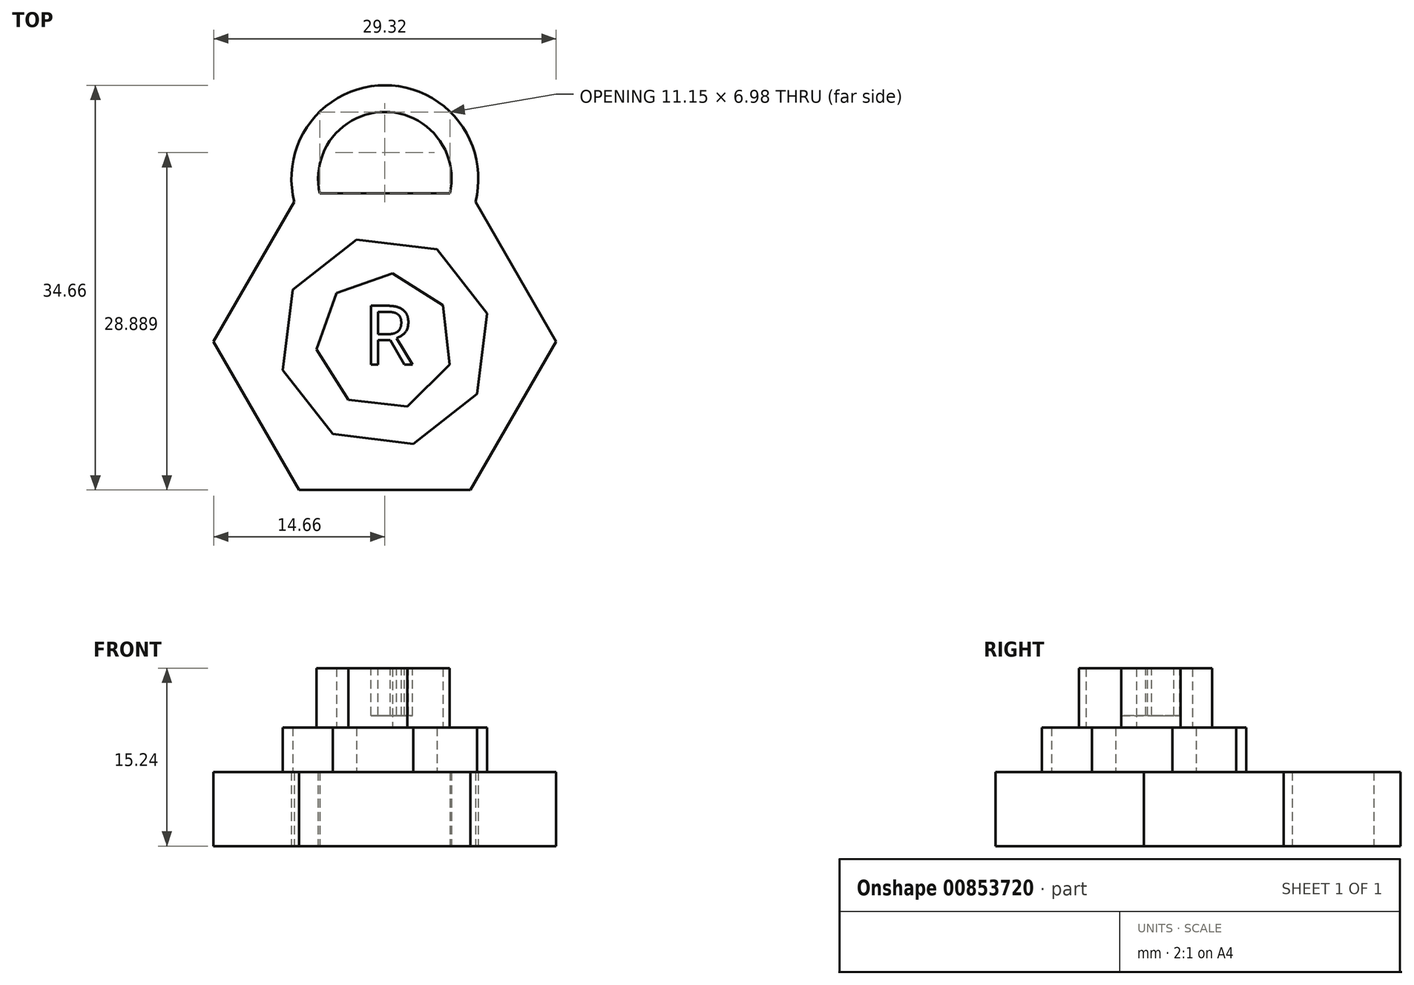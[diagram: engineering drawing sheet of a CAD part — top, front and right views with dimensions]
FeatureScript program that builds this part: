
annotation { "Feature Type Name" : "Feature", "Feature Type Description" : "" }
export const myFeature = defineFeature(function(context is Context, id is Id, definition is map)
    precondition{}
    {
        {
            var Q0;
            Q0=qCreatedBy(makeId("Top.planeOp"),FACE);
            var sketch = newSketch(context, id + "F0", { "sketchPlane" : qUnion([Q0])});
            skCircle(sketch, "E0.cCircle", {"center": v(0, 0) * mm, "radius": 12.7 * mm, "construction": true});
            skLineSegment(sketch, "E0.0", {"start": v(-7.33, 12.7) * mm, "end": v(7.33, 12.7) * mm});
            skLineSegment(sketch, "E0.1", {"start": v(7.33, 12.7) * mm, "end": v(14.66, 0) * mm});
            skLineSegment(sketch, "E0.2", {"start": v(14.66, 0) * mm, "end": v(7.33, -12.7) * mm});
            skLineSegment(sketch, "E0.3", {"start": v(7.33, -12.7) * mm, "end": v(-7.33, -12.7) * mm});
            skLineSegment(sketch, "E0.4", {"start": v(-7.33, -12.7) * mm, "end": v(-14.66, 0) * mm});
            skLineSegment(sketch, "E0.5", {"start": v(-14.66, 0) * mm, "end": v(-7.33, 12.7) * mm});
            skPoint(sketch, "E0.0.midPoint", {"position": v(0, 12.7) * mm});
            skSolve(sketch);
        }
        {
            var Q0;
            Q0=makeQuery(id+"F0.imprint","IMPRINT",FACE,{"disambiguationData":[TD([[makeQuery(id+"F0.imprint","IMPRINT",EDGE,{"derivedFrom":sQuery(id+"F0.wireOp",EDGE,"E0.0")}),-1.0]])]});
            extrude(context, id + "F1", {"entities" : qUnion([Q0]), "depth" : 6.35 * mm, "offsetDistance" : 25.4 * mm});
        }
        {
            var Q0;
            Q0=makeQuery(id+"F1.opExtrude","CAP_FACE",FACE,{"disambiguationData":[OSD([sQuery(id+"F0.wireOp",EDGE,"E0.0"),sQuery(id+"F0.wireOp",EDGE,"E0.1"),sQuery(id+"F0.wireOp",EDGE,"E0.2"),sQuery(id+"F0.wireOp",EDGE,"E0.3"),sQuery(id+"F0.wireOp",EDGE,"E0.4"),sQuery(id+"F0.wireOp",EDGE,"E0.5")])],"isStart":false});
            var sketch = newSketch(context, id + "F2", { "sketchPlane" : qUnion([Q0])});
            skCircle(sketch, "E1.cCircle", {"center": v(0, 0) * mm, "radius": 8.38 * mm, "construction": true});
            skLineSegment(sketch, "E1.0", {"start": v(7.9, -4.46) * mm, "end": v(2.44, -8.74) * mm});
            skLineSegment(sketch, "E1.1", {"start": v(2.44, -8.74) * mm, "end": v(-4.46, -7.9) * mm});
            skLineSegment(sketch, "E1.2", {"start": v(-4.46, -7.9) * mm, "end": v(-8.74, -2.44) * mm});
            skLineSegment(sketch, "E1.3", {"start": v(-8.74, -2.44) * mm, "end": v(-7.9, 4.46) * mm});
            skLineSegment(sketch, "E1.4", {"start": v(-7.9, 4.46) * mm, "end": v(-2.44, 8.74) * mm});
            skLineSegment(sketch, "E1.5", {"start": v(-2.44, 8.74) * mm, "end": v(4.46, 7.9) * mm});
            skLineSegment(sketch, "E1.6", {"start": v(4.46, 7.9) * mm, "end": v(8.74, 2.44) * mm});
            skLineSegment(sketch, "E1.7", {"start": v(8.74, 2.44) * mm, "end": v(7.9, -4.46) * mm});
            skPoint(sketch, "E1.0.midPoint", {"position": v(5.17, -6.6) * mm});
            skSolve(sketch);
        }
        {
            var Q0;
            Q0 = qSketchRegion(id + "F2", true);
            extrude(context, id + "F3", {"entities" : qUnion([Q0]), "operationType" : NewBodyOperationType.ADD, "depth" : 3.8 * mm, "offsetDistance" : 25.4 * mm});
        }
        {
            var Q0;
            Q0=makeQuery(id+"F3.opExtrude","CAP_FACE",FACE,{"disambiguationData":[OSD([sQuery(id+"F2.wireOp",EDGE,"E1.0"),sQuery(id+"F2.wireOp",EDGE,"E1.1"),sQuery(id+"F2.wireOp",EDGE,"E1.2"),sQuery(id+"F2.wireOp",EDGE,"E1.3"),sQuery(id+"F2.wireOp",EDGE,"E1.4"),sQuery(id+"F2.wireOp",EDGE,"E1.5"),sQuery(id+"F2.wireOp",EDGE,"E1.6"),sQuery(id+"F2.wireOp",EDGE,"E1.7")])],"isStart":false});
            var sketch = newSketch(context, id + "F4", { "sketchPlane" : qUnion([Q0])});
            skCircle(sketch, "E2.cCircle", {"center": v(0, 0) * mm, "radius": 5.3 * mm, "construction": true});
            skLineSegment(sketch, "E2.0", {"start": v(5.55, -1.95) * mm, "end": v(1.93, -5.55) * mm});
            skLineSegment(sketch, "E2.1", {"start": v(1.93, -5.55) * mm, "end": v(-3.13, -4.97) * mm});
            skLineSegment(sketch, "E2.2", {"start": v(-3.13, -4.97) * mm, "end": v(-5.84, -0.65) * mm});
            skLineSegment(sketch, "E2.3", {"start": v(-5.84, -0.65) * mm, "end": v(-4.15, 4.16) * mm});
            skLineSegment(sketch, "E2.4", {"start": v(-4.15, 4.16) * mm, "end": v(0.67, 5.84) * mm});
            skLineSegment(sketch, "E2.5", {"start": v(0.67, 5.84) * mm, "end": v(4.98, 3.12) * mm});
            skLineSegment(sketch, "E2.6", {"start": v(4.98, 3.12) * mm, "end": v(5.55, -1.95) * mm});
            skPoint(sketch, "E2.0.midPoint", {"position": v(3.74, -3.75) * mm});
            skSolve(sketch);
        }
        {
            var Q0;
            Q0 = qSketchRegion(id + "F4", true);
            extrude(context, id + "F5", {"entities" : qUnion([Q0]), "operationType" : NewBodyOperationType.ADD, "depth" : 5.08 * mm, "offsetDistance" : 25.4 * mm});
        }
        {
            var Q0;
            Q0=makeQuery(id+"F5.opExtrude","CAP_FACE",FACE,{"disambiguationData":[OSD([sQuery(id+"F4.wireOp",EDGE,"E2.0"),sQuery(id+"F4.wireOp",EDGE,"E2.1"),sQuery(id+"F4.wireOp",EDGE,"E2.2"),sQuery(id+"F4.wireOp",EDGE,"E2.3"),sQuery(id+"F4.wireOp",EDGE,"E2.4"),sQuery(id+"F4.wireOp",EDGE,"E2.5"),sQuery(id+"F4.wireOp",EDGE,"E2.6")])],"isStart":false});
            var sketch = newSketch(context, id + "F6", { "sketchPlane" : qUnion([Q0])});
            skText(sketch, "E3", { "text": "R", "fontName": "OpenSans-Regular.ttf"});
            skPoint(sketch, "E3.secondSnap0", {"position": v(2.82, 4.48) * mm});
            const initialGuessF6  = {"E3": [-0.00187, -0.00195, 1, 0, 0.00507]};
            skSetInitialGuess(sketch, initialGuessF6);
            skSolve(sketch);
        }
        {
            var Q0;
            Q0 = qSketchRegion(id + "F6", true);
            extrude(context, id + "F7", {"entities" : qUnion([Q0]), "operationType" : NewBodyOperationType.REMOVE, "oppositeDirection" : true, "depth" : 4.06 * mm, "offsetDistance" : 25.4 * mm});
        }
        {
            var Q0;
            Q0=makeQuery(id+"F1.opExtrude","CAP_FACE",FACE,{"disambiguationData":[OSD([sQuery(id+"F0.wireOp",EDGE,"E0.0"),sQuery(id+"F0.wireOp",EDGE,"E0.1"),sQuery(id+"F0.wireOp",EDGE,"E0.2"),sQuery(id+"F0.wireOp",EDGE,"E0.3"),sQuery(id+"F0.wireOp",EDGE,"E0.4"),sQuery(id+"F0.wireOp",EDGE,"E0.5")])],"isStart":true});
            var sketch = newSketch(context, id + "F8", { "sketchPlane" : qUnion([Q0])});
            skCircle(sketch, "E4", {"center": v(0, -13.96) * mm, "radius": 5.72 * mm});
            skCircle(sketch, "E5", {"center": v(0, -13.96) * mm, "radius": 8 * mm});
            skPoint(sketch, "E6", {"position": v(0, -12.7) * mm});
            skSolve(sketch);
        }
        {
            var Q0;
            {var subQ1=makeQuery(id+"F1.opExtrude","CAP_EDGE",EDGE,{"disambiguationData":[OSD([sQuery(id+"F0.wireOp",EDGE,"E0.0")])],"isStart":true});var subQ3=sQuery(id+"F8.wireOp",EDGE,"E4");var subQ4=makeQuery(id+"F8.imprint","INTERSECT",VERTEX,{"disambiguationData":[OD(0.0)],"derivedFrom":[subQ1,subQ3]});Q0=makeQuery(id+"F8.imprint","IMPRINT",FACE,{"disambiguationData":[TD([[makeQuery(id+"F8.imprint","IMPRINT",EDGE,{"disambiguationData":[TD([[subQ4,-1.0]])],"derivedFrom":subQ3}),-1.0]])]});}
            extrude(context, id + "F9", {"entities" : qUnion([Q0]), "operationType" : NewBodyOperationType.ADD, "oppositeDirection" : true, "depth" : 6.35 * mm, "offsetDistance" : 25.4 * mm});
        }
    });
